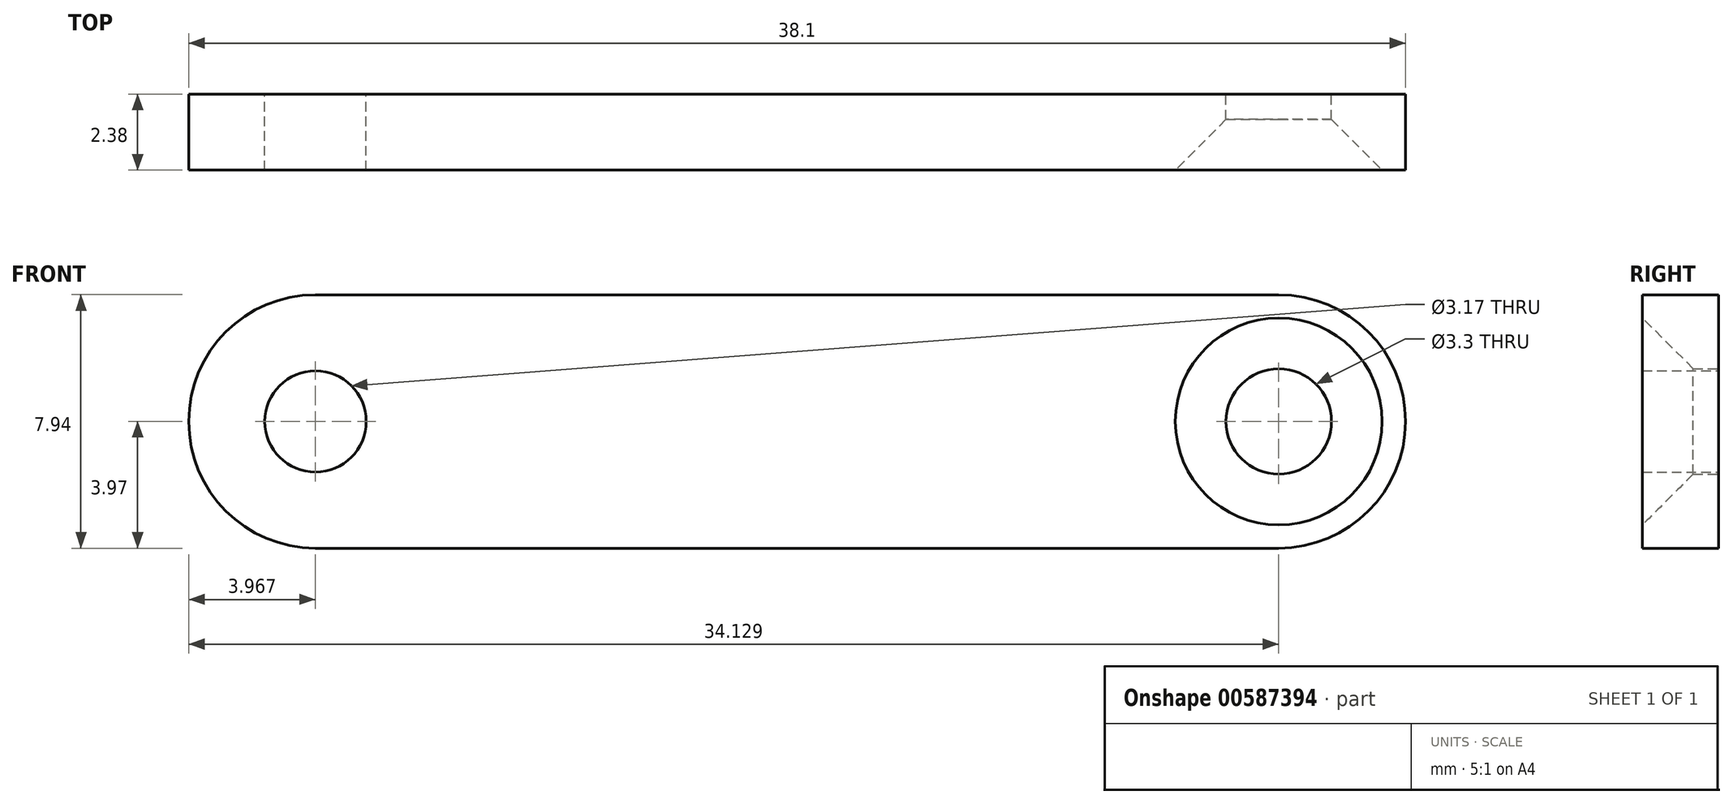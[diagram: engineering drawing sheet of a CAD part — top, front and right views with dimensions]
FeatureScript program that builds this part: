
annotation { "Feature Type Name" : "Feature", "Feature Type Description" : "" }
export const myFeature = defineFeature(function(context is Context, id is Id, definition is map)
    precondition{}
    {
        {
            var Q0;
            Q0=qCreatedBy(makeId("Front.planeOp"),FACE);
            var sketch = newSketch(context, id + "F0", { "sketchPlane" : qUnion([Q0])});
            skLineSegment(sketch, "E0", {"start": v(-18.05, 0) * mm, "end": v(21.49, 0) * mm, "construction": true});
            skLineSegment(sketch, "E1", {"start": v(-12.9, 6.97) * mm, "end": v(-12.9, -14.9) * mm, "construction": true});
            skLineSegment(sketch, "E2", {"start": v(17.27, 8.06) * mm, "end": v(17.27, -14.9) * mm, "construction": true});
            skLineSegment(sketch, "E3", {"start": v(-12.9, 3.97) * mm, "end": v(17.27, 3.97) * mm});
            skLineSegment(sketch, "E4", {"start": v(-12.9, -3.97) * mm, "end": v(17.27, -3.97) * mm});
            skArc(sketch, "E5", {"start": v(17.27, 3.97) * mm, "mid": v(21.24, 0) * mm, "end": v(17.27, -3.97) * mm});
            skArc(sketch, "E6", {"start": v(-12.9, 3.97) * mm, "mid": v(-16.86, 0) * mm, "end": v(-12.9, -3.97) * mm});
            skCircle(sketch, "E7", {"center": v(-12.9, 0) * mm, "radius": 1.59 * mm});
            skCircle(sketch, "E8", {"center": v(17.27, 0) * mm, "radius": 1.65 * mm});
            skSolve(sketch);
        }
        {
            var Q0;
            Q0=makeQuery(id+"F0.imprint","IMPRINT",FACE,{"disambiguationData":[TD([[makeQuery(id+"F0.imprint","IMPRINT",EDGE,{"derivedFrom":sQuery(id+"F0.wireOp",EDGE,"E3")}),-1.0]])]});
            extrude(context, id + "F1", {"entities" : qUnion([Q0]), "depth" : 2.38 * mm, "offsetDistance" : 25.4 * mm});
        }
        {
            var Q0;
            Q0=makeQuery(id+"F1.opExtrude","CAP_EDGE",EDGE,{"disambiguationData":[OSD([sQuery(id+"F0.wireOp",EDGE,"E8")])],"isStart":false});
            chamfer(context, id + "F2", {"entities" : qUnion([Q0]), "chamferType" : ChamferType.OFFSET_ANGLE, "width" : 1.59 * mm, "oppositeDirection" : false, "angle" : 45 * degree, "tangentPropagation" : true});
        }
    });
